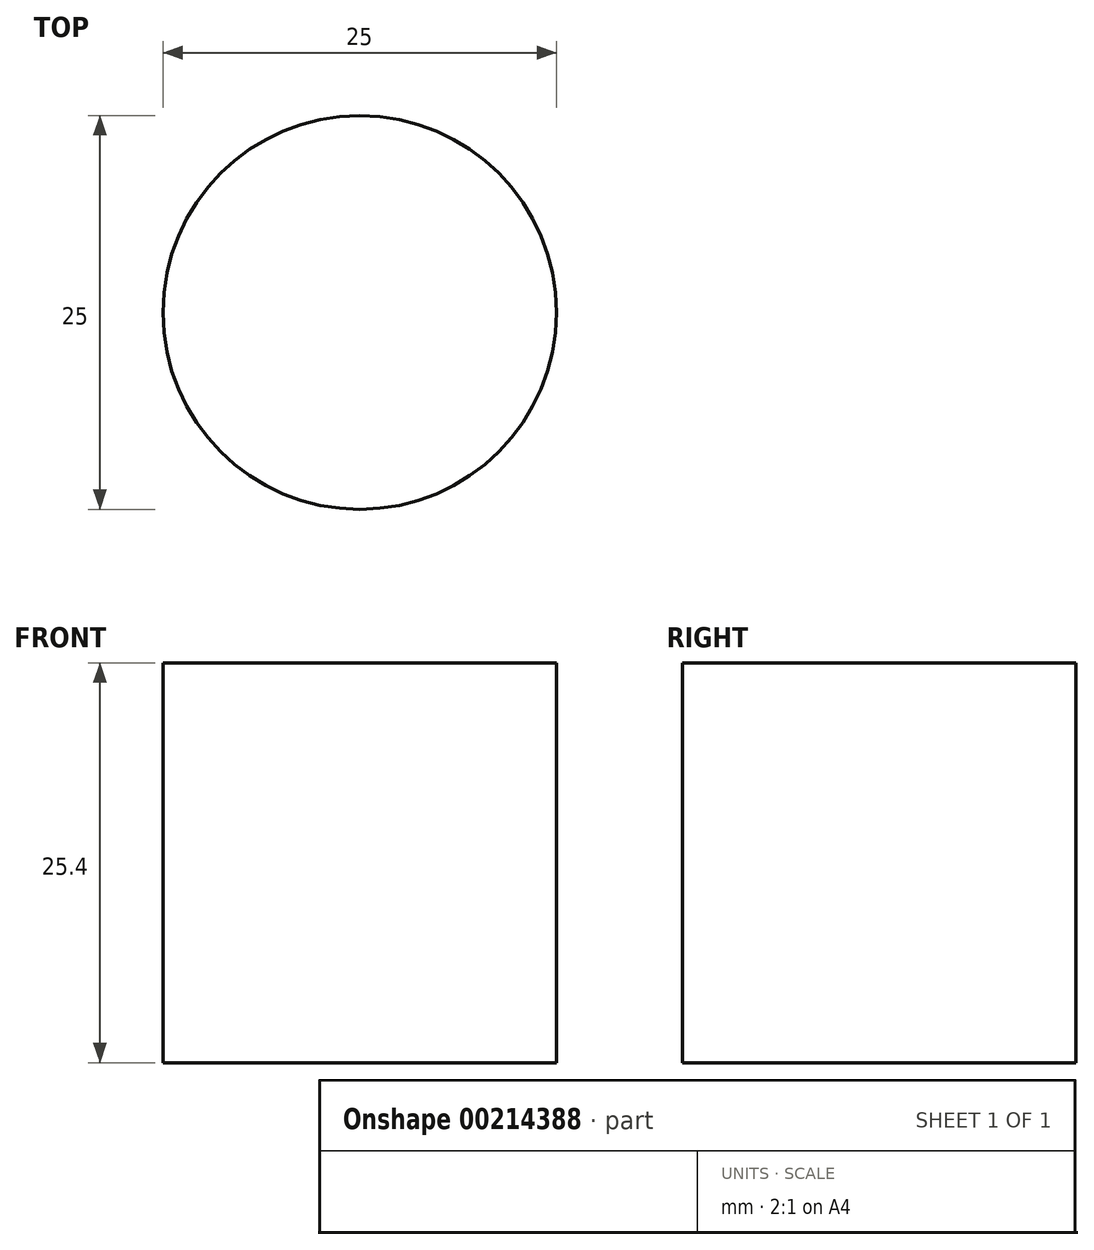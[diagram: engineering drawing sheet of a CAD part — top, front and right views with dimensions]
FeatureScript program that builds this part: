
annotation { "Feature Type Name" : "Feature", "Feature Type Description" : "" }
export const myFeature = defineFeature(function(context is Context, id is Id, definition is map)
    precondition{}
    {
        {
            var Q0;
            Q0=qCreatedBy(makeId("Top.planeOp"),FACE);
            var sketch = newSketch(context, id + "F0", { "sketchPlane" : qUnion([Q0])});
            skCircle(sketch, "E0", {"center": v(0, 0) * mm, "radius": 12 * mm});
            skCircle(sketch, "E1", {"center": v(0, 0) * mm, "radius": 12.5 * mm});
            skSolve(sketch);
        }
        {
            var Q0;
            Q0=makeQuery(id+"F0.imprint","IMPRINT",FACE,{"disambiguationData":[TD([[makeQuery(id+"F0.imprint","IMPRINT",EDGE,{"derivedFrom":sQuery(id+"F0.wireOp",EDGE,"E0")}),1.0]])]});
            var Q1;
            Q1=makeQuery(id+"F0.imprint","IMPRINT",FACE,{"disambiguationData":[TD([[makeQuery(id+"F0.imprint","IMPRINT",EDGE,{"derivedFrom":sQuery(id+"F0.wireOp",EDGE,"E0")}),-1.0]])]});
            extrude(context, id + "F1", {"entities" : qUnion([Q0, Q1]), "depth" : 25.4 * mm});
        }
    });
